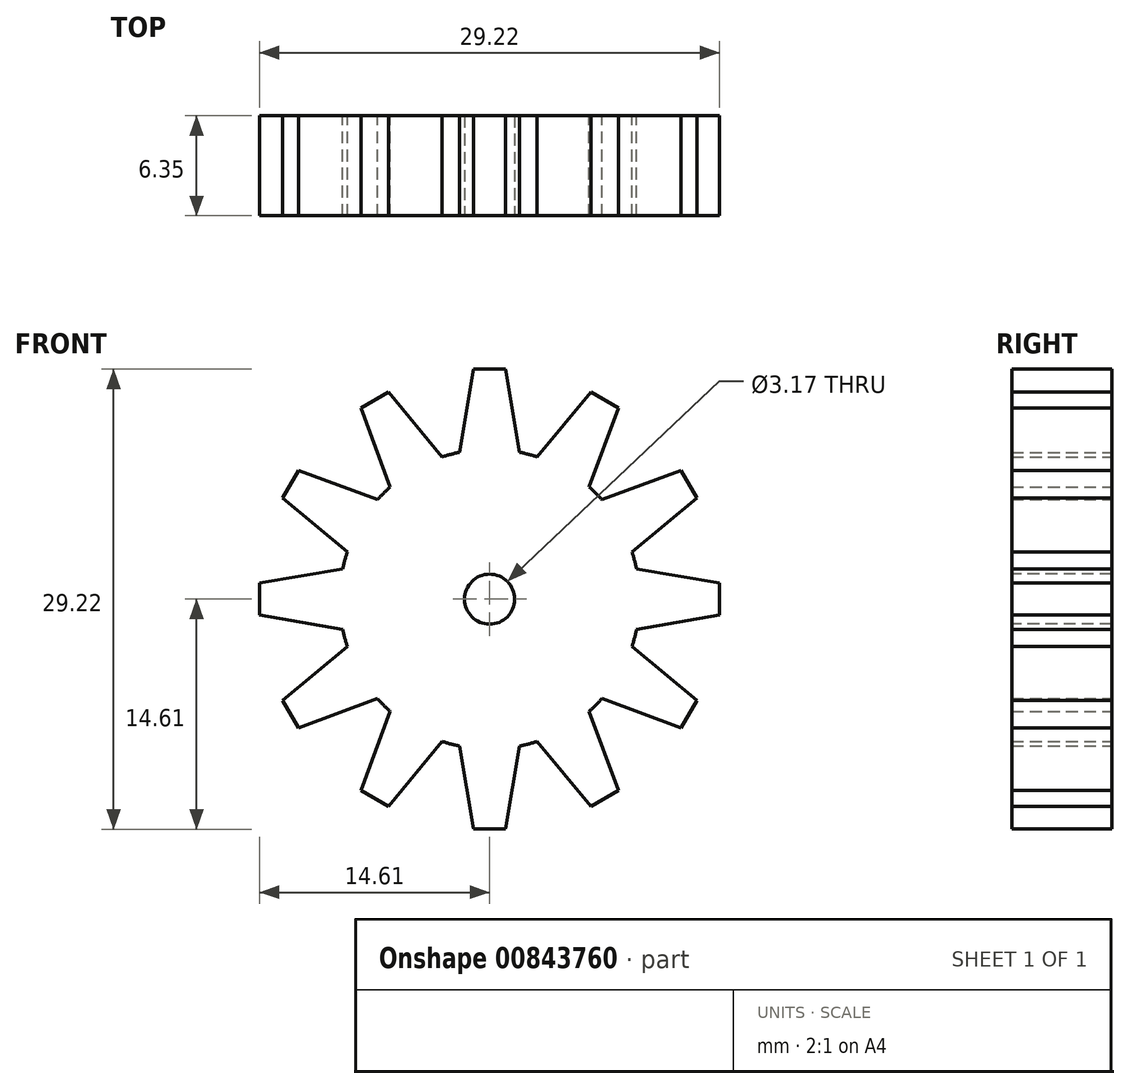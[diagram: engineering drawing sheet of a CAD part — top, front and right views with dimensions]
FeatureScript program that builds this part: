
annotation { "Feature Type Name" : "Feature", "Feature Type Description" : "" }
export const myFeature = defineFeature(function(context is Context, id is Id, definition is map)
    precondition{}
    {
        {
            var Q0;
            Q0=qCreatedBy(makeId("Front.planeOp"),FACE);
            var sketch = newSketch(context, id + "F0", { "sketchPlane" : qUnion([Q0])});
            skCircle(sketch, "E0", {"center": v(0, 0) * mm, "radius": 9.53 * mm});
            skLineSegment(sketch, "E1", {"start": v(0, 14.6) * mm, "end": v(0, 0) * mm});
            skLineSegment(sketch, "E2", {"start": v(0, 14.6) * mm, "end": v(-1.02, 14.6) * mm});
            skLineSegment(sketch, "E3", {"start": v(-1.02, 14.6) * mm, "end": v(-1.9, 9.33) * mm});
            skLineSegment(sketch, "E4.MirrorCS", {"start": v(1.02, 14.6) * mm, "end": v(1.9, 9.33) * mm});
            skLineSegment(sketch, "E5.MirrorCS", {"start": v(0, 14.6) * mm, "end": v(1.02, 14.6) * mm});
            skLineSegment(sketch, "E6.1.1", {"start": v(-6.42, 13.16) * mm, "end": v(-3.01, 9.04) * mm});
            skLineSegment(sketch, "E6.1.2", {"start": v(-7.3, 12.65) * mm, "end": v(-6.42, 13.16) * mm});
            skLineSegment(sketch, "E6.1.3", {"start": v(-7.3, 12.65) * mm, "end": v(-8.18, 12.14) * mm});
            skLineSegment(sketch, "E6.1.4", {"start": v(-8.18, 12.14) * mm, "end": v(-6.32, 7.13) * mm});
            skLineSegment(sketch, "E6.2.1", {"start": v(-12.14, 8.18) * mm, "end": v(-7.13, 6.32) * mm});
            skLineSegment(sketch, "E6.2.2", {"start": v(-12.65, 7.3) * mm, "end": v(-12.14, 8.18) * mm});
            skLineSegment(sketch, "E6.2.3", {"start": v(-12.65, 7.3) * mm, "end": v(-13.16, 6.42) * mm});
            skLineSegment(sketch, "E6.2.4", {"start": v(-13.16, 6.42) * mm, "end": v(-9.04, 3.01) * mm});
            skLineSegment(sketch, "E7.2.3.0", {"start": v(-14.6, 1.02) * mm, "end": v(-9.33, 1.9) * mm});
            skLineSegment(sketch, "E7.5.3.0", {"start": v(-14.6, 0) * mm, "end": v(-14.6, 1.02) * mm});
            skLineSegment(sketch, "E7.8.3.0", {"start": v(-14.6, 0) * mm, "end": v(-14.6, -1.02) * mm});
            skLineSegment(sketch, "E7.11.3.0", {"start": v(-14.6, -1.02) * mm, "end": v(-9.33, -1.9) * mm});
            skLineSegment(sketch, "E7.2.4.0", {"start": v(-13.16, -6.42) * mm, "end": v(-9.04, -3.01) * mm});
            skLineSegment(sketch, "E7.5.4.0", {"start": v(-12.65, -7.3) * mm, "end": v(-13.16, -6.42) * mm});
            skLineSegment(sketch, "E7.8.4.0", {"start": v(-12.65, -7.3) * mm, "end": v(-12.14, -8.18) * mm});
            skLineSegment(sketch, "E7.11.4.0", {"start": v(-12.14, -8.18) * mm, "end": v(-7.13, -6.32) * mm});
            skLineSegment(sketch, "E7.2.5.0", {"start": v(-8.18, -12.14) * mm, "end": v(-6.32, -7.13) * mm});
            skLineSegment(sketch, "E7.5.5.0", {"start": v(-7.3, -12.65) * mm, "end": v(-8.18, -12.14) * mm});
            skLineSegment(sketch, "E7.8.5.0", {"start": v(-7.3, -12.65) * mm, "end": v(-6.42, -13.16) * mm});
            skLineSegment(sketch, "E7.11.5.0", {"start": v(-6.42, -13.16) * mm, "end": v(-3.01, -9.04) * mm});
            skLineSegment(sketch, "E7.2.6.0", {"start": v(-1.02, -14.6) * mm, "end": v(-1.9, -9.33) * mm});
            skLineSegment(sketch, "E7.5.6.0", {"start": v(0, -14.6) * mm, "end": v(-1.02, -14.6) * mm});
            skLineSegment(sketch, "E7.8.6.0", {"start": v(0, -14.6) * mm, "end": v(1.02, -14.6) * mm});
            skLineSegment(sketch, "E7.11.6.0", {"start": v(1.02, -14.6) * mm, "end": v(1.9, -9.33) * mm});
            skLineSegment(sketch, "E7.2.7.0", {"start": v(6.42, -13.16) * mm, "end": v(3.01, -9.04) * mm});
            skLineSegment(sketch, "E7.5.7.0", {"start": v(7.3, -12.65) * mm, "end": v(6.42, -13.16) * mm});
            skLineSegment(sketch, "E7.8.7.0", {"start": v(7.3, -12.65) * mm, "end": v(8.18, -12.14) * mm});
            skLineSegment(sketch, "E7.11.7.0", {"start": v(8.18, -12.14) * mm, "end": v(6.32, -7.13) * mm});
            skLineSegment(sketch, "E7.2.8.0", {"start": v(12.14, -8.18) * mm, "end": v(7.13, -6.32) * mm});
            skLineSegment(sketch, "E7.5.8.0", {"start": v(12.65, -7.3) * mm, "end": v(12.14, -8.18) * mm});
            skLineSegment(sketch, "E7.8.8.0", {"start": v(12.65, -7.3) * mm, "end": v(13.16, -6.42) * mm});
            skLineSegment(sketch, "E7.11.8.0", {"start": v(13.16, -6.42) * mm, "end": v(9.04, -3.01) * mm});
            skLineSegment(sketch, "E7.2.9.0", {"start": v(14.6, -1.02) * mm, "end": v(9.33, -1.9) * mm});
            skLineSegment(sketch, "E7.5.9.0", {"start": v(14.6, 0) * mm, "end": v(14.6, -1.02) * mm});
            skLineSegment(sketch, "E7.8.9.0", {"start": v(14.6, 0) * mm, "end": v(14.6, 1.02) * mm});
            skLineSegment(sketch, "E7.11.9.0", {"start": v(14.6, 1.02) * mm, "end": v(9.33, 1.9) * mm});
            skLineSegment(sketch, "E7.2.10.0", {"start": v(13.16, 6.42) * mm, "end": v(9.04, 3.01) * mm});
            skLineSegment(sketch, "E7.5.10.0", {"start": v(12.65, 7.3) * mm, "end": v(13.16, 6.42) * mm});
            skLineSegment(sketch, "E7.8.10.0", {"start": v(12.65, 7.3) * mm, "end": v(12.14, 8.18) * mm});
            skLineSegment(sketch, "E7.11.10.0", {"start": v(12.14, 8.18) * mm, "end": v(7.13, 6.32) * mm});
            skLineSegment(sketch, "E7.2.11.0", {"start": v(8.18, 12.14) * mm, "end": v(6.32, 7.13) * mm});
            skLineSegment(sketch, "E7.5.11.0", {"start": v(7.3, 12.65) * mm, "end": v(8.18, 12.14) * mm});
            skLineSegment(sketch, "E7.8.11.0", {"start": v(7.3, 12.65) * mm, "end": v(6.42, 13.16) * mm});
            skLineSegment(sketch, "E7.11.11.0", {"start": v(6.42, 13.16) * mm, "end": v(3.01, 9.04) * mm});
            skSolve(sketch);
        }
        {
            var Q0;
            {var subQ1=sQuery(id+"F0.wireOp",EDGE,"E6.1.1");Q0=makeQuery(id+"F0.imprint","IMPRINT",FACE,{"disambiguationData":[TD([[makeQuery(id+"F0.imprint","IMPRINT",EDGE,{"derivedFrom":subQ1}),-1.0]])]});}
            var Q1;
            {var subQ1=sQuery(id+"F0.wireOp",EDGE,"E6.2.1");Q1=makeQuery(id+"F0.imprint","IMPRINT",FACE,{"disambiguationData":[TD([[makeQuery(id+"F0.imprint","IMPRINT",EDGE,{"derivedFrom":subQ1}),-1.0]])]});}
            var Q2;
            {var subQ2=sQuery(id+"F0.wireOp",EDGE,"E7.2.3.0");Q2=makeQuery(id+"F0.imprint","IMPRINT",FACE,{"disambiguationData":[TD([[makeQuery(id+"F0.imprint","IMPRINT",EDGE,{"derivedFrom":subQ2}),-1.0]])]});}
            var Q3;
            {var subQ1=sQuery(id+"F0.wireOp",EDGE,"E7.2.5.0");Q3=makeQuery(id+"F0.imprint","IMPRINT",FACE,{"disambiguationData":[TD([[makeQuery(id+"F0.imprint","IMPRINT",EDGE,{"derivedFrom":subQ1}),-1.0]])]});}
            var Q4;
            {var subQ2=sQuery(id+"F0.wireOp",EDGE,"E7.2.4.0");Q4=makeQuery(id+"F0.imprint","IMPRINT",FACE,{"disambiguationData":[TD([[makeQuery(id+"F0.imprint","IMPRINT",EDGE,{"derivedFrom":subQ2}),-1.0]])]});}
            var Q5;
            {var subQ0=sQuery(id+"F0.wireOp",EDGE,"E0");var subQ18=makeQuery(id+"F0.imprint","INTERSECT",VERTEX,{"derivedFrom":[sQuery(id+"F0.wireOp",EDGE,"E7.11.8.0"),subQ0]});Q5=makeQuery(id+"F0.imprint","IMPRINT",FACE,{"disambiguationData":[TD([[makeQuery(id+"F0.imprint","IMPRINT",EDGE,{"disambiguationData":[TD([[subQ18,-1.0]])],"derivedFrom":subQ0}),1.0]])]});}
            var Q6;
            {var subQ1=sQuery(id+"F0.wireOp",EDGE,"E7.2.6.0");Q6=makeQuery(id+"F0.imprint","IMPRINT",FACE,{"disambiguationData":[TD([[makeQuery(id+"F0.imprint","IMPRINT",EDGE,{"derivedFrom":subQ1}),-1.0]])]});}
            var Q7;
            {var subQ1=sQuery(id+"F0.wireOp",EDGE,"E7.2.7.0");Q7=makeQuery(id+"F0.imprint","IMPRINT",FACE,{"disambiguationData":[TD([[makeQuery(id+"F0.imprint","IMPRINT",EDGE,{"derivedFrom":subQ1}),-1.0]])]});}
            var Q8;
            {var subQ1=sQuery(id+"F0.wireOp",EDGE,"E7.2.8.0");Q8=makeQuery(id+"F0.imprint","IMPRINT",FACE,{"disambiguationData":[TD([[makeQuery(id+"F0.imprint","IMPRINT",EDGE,{"derivedFrom":subQ1}),-1.0]])]});}
            var Q9;
            {var subQ1=sQuery(id+"F0.wireOp",EDGE,"E7.2.9.0");Q9=makeQuery(id+"F0.imprint","IMPRINT",FACE,{"disambiguationData":[TD([[makeQuery(id+"F0.imprint","IMPRINT",EDGE,{"derivedFrom":subQ1}),-1.0]])]});}
            var Q10;
            {var subQ1=sQuery(id+"F0.wireOp",EDGE,"E7.2.10.0");Q10=makeQuery(id+"F0.imprint","IMPRINT",FACE,{"disambiguationData":[TD([[makeQuery(id+"F0.imprint","IMPRINT",EDGE,{"derivedFrom":subQ1}),-1.0]])]});}
            var Q11;
            {var subQ1=sQuery(id+"F0.wireOp",EDGE,"E7.2.11.0");Q11=makeQuery(id+"F0.imprint","IMPRINT",FACE,{"disambiguationData":[TD([[makeQuery(id+"F0.imprint","IMPRINT",EDGE,{"derivedFrom":subQ1}),-1.0]])]});}
            var Q12;
            {var subQ0=sQuery(id+"F0.wireOp",EDGE,"E2");Q12=makeQuery(id+"F0.imprint","IMPRINT",FACE,{"disambiguationData":[TD([[makeQuery(id+"F0.imprint","IMPRINT",EDGE,{"derivedFrom":subQ0}),1.0]])]});}
            var Q13;
            {var subQ4=sQuery(id+"F0.wireOp",EDGE,"E4.MirrorCS");Q13=makeQuery(id+"F0.imprint","IMPRINT",FACE,{"disambiguationData":[TD([[makeQuery(id+"F0.imprint","IMPRINT",EDGE,{"derivedFrom":subQ4}),-1.0]])]});}
            extrude(context, id + "F1", {"entities" : qUnion([Q0, Q1, Q2, Q3, Q4, Q5, Q6, Q7, Q8, Q9, Q10, Q11, Q12, Q13]), "depth" : 6.35 * mm, "offsetDistance" : 25.4 * mm});
        }
        {
            var Q0;
            Q0=makeQuery(id+"F1.opExtrude","CAP_FACE",FACE,{"disambiguationData":[OSD([sQuery(id+"F0.wireOp",EDGE,"E2"),sQuery(id+"F0.wireOp",EDGE,"E3"),sQuery(id+"F0.wireOp",EDGE,"E4.MirrorCS"),sQuery(id+"F0.wireOp",EDGE,"E5.MirrorCS"),sQuery(id+"F0.wireOp",EDGE,"E6.1.1"),sQuery(id+"F0.wireOp",EDGE,"E6.1.2"),sQuery(id+"F0.wireOp",EDGE,"E6.1.3"),sQuery(id+"F0.wireOp",EDGE,"E6.1.4"),sQuery(id+"F0.wireOp",EDGE,"E6.2.1"),sQuery(id+"F0.wireOp",EDGE,"E6.2.2"),sQuery(id+"F0.wireOp",EDGE,"E6.2.3"),sQuery(id+"F0.wireOp",EDGE,"E6.2.4"),sQuery(id+"F0.wireOp",EDGE,"E7.2.3.0"),sQuery(id+"F0.wireOp",EDGE,"E7.5.3.0"),sQuery(id+"F0.wireOp",EDGE,"E7.8.3.0"),sQuery(id+"F0.wireOp",EDGE,"E7.11.3.0"),sQuery(id+"F0.wireOp",EDGE,"E7.2.4.0"),sQuery(id+"F0.wireOp",EDGE,"E7.5.4.0"),sQuery(id+"F0.wireOp",EDGE,"E7.8.4.0"),sQuery(id+"F0.wireOp",EDGE,"E7.11.4.0"),sQuery(id+"F0.wireOp",EDGE,"E7.2.5.0"),sQuery(id+"F0.wireOp",EDGE,"E7.5.5.0"),sQuery(id+"F0.wireOp",EDGE,"E7.8.5.0"),sQuery(id+"F0.wireOp",EDGE,"E7.11.5.0"),sQuery(id+"F0.wireOp",EDGE,"E7.2.6.0"),sQuery(id+"F0.wireOp",EDGE,"E7.5.6.0"),sQuery(id+"F0.wireOp",EDGE,"E7.8.6.0"),sQuery(id+"F0.wireOp",EDGE,"E7.11.6.0"),sQuery(id+"F0.wireOp",EDGE,"E7.2.7.0"),sQuery(id+"F0.wireOp",EDGE,"E7.5.7.0"),sQuery(id+"F0.wireOp",EDGE,"E7.8.7.0"),sQuery(id+"F0.wireOp",EDGE,"E7.11.7.0"),sQuery(id+"F0.wireOp",EDGE,"E7.2.8.0"),sQuery(id+"F0.wireOp",EDGE,"E7.5.8.0"),sQuery(id+"F0.wireOp",EDGE,"E7.8.8.0"),sQuery(id+"F0.wireOp",EDGE,"E7.11.8.0"),sQuery(id+"F0.wireOp",EDGE,"E7.2.9.0"),sQuery(id+"F0.wireOp",EDGE,"E7.5.9.0"),sQuery(id+"F0.wireOp",EDGE,"E7.8.9.0"),sQuery(id+"F0.wireOp",EDGE,"E7.11.9.0"),sQuery(id+"F0.wireOp",EDGE,"E7.2.10.0"),sQuery(id+"F0.wireOp",EDGE,"E7.5.10.0"),sQuery(id+"F0.wireOp",EDGE,"E7.8.10.0"),sQuery(id+"F0.wireOp",EDGE,"E7.11.10.0"),sQuery(id+"F0.wireOp",EDGE,"E7.2.11.0"),sQuery(id+"F0.wireOp",EDGE,"E0"),sQuery(id+"F0.wireOp",EDGE,"E7.5.11.0"),sQuery(id+"F0.wireOp",EDGE,"E7.8.11.0"),sQuery(id+"F0.wireOp",EDGE,"E7.11.11.0")])],"isStart":false});
            var sketch = newSketch(context, id + "F2", { "sketchPlane" : qUnion([Q0])});
            skCircle(sketch, "E8", {"center": v(0, 0) * mm, "radius": 1.59 * mm});
            skSolve(sketch);
        }
        {
            var Q0;
            Q0 = qSketchRegion(id + "F2", true);
            extrude(context, id + "F3", {"entities" : qUnion([Q0]), "operationType" : NewBodyOperationType.REMOVE, "oppositeDirection" : true, "depth" : 6.35 * mm, "offsetDistance" : 25.4 * mm});
        }
    });
